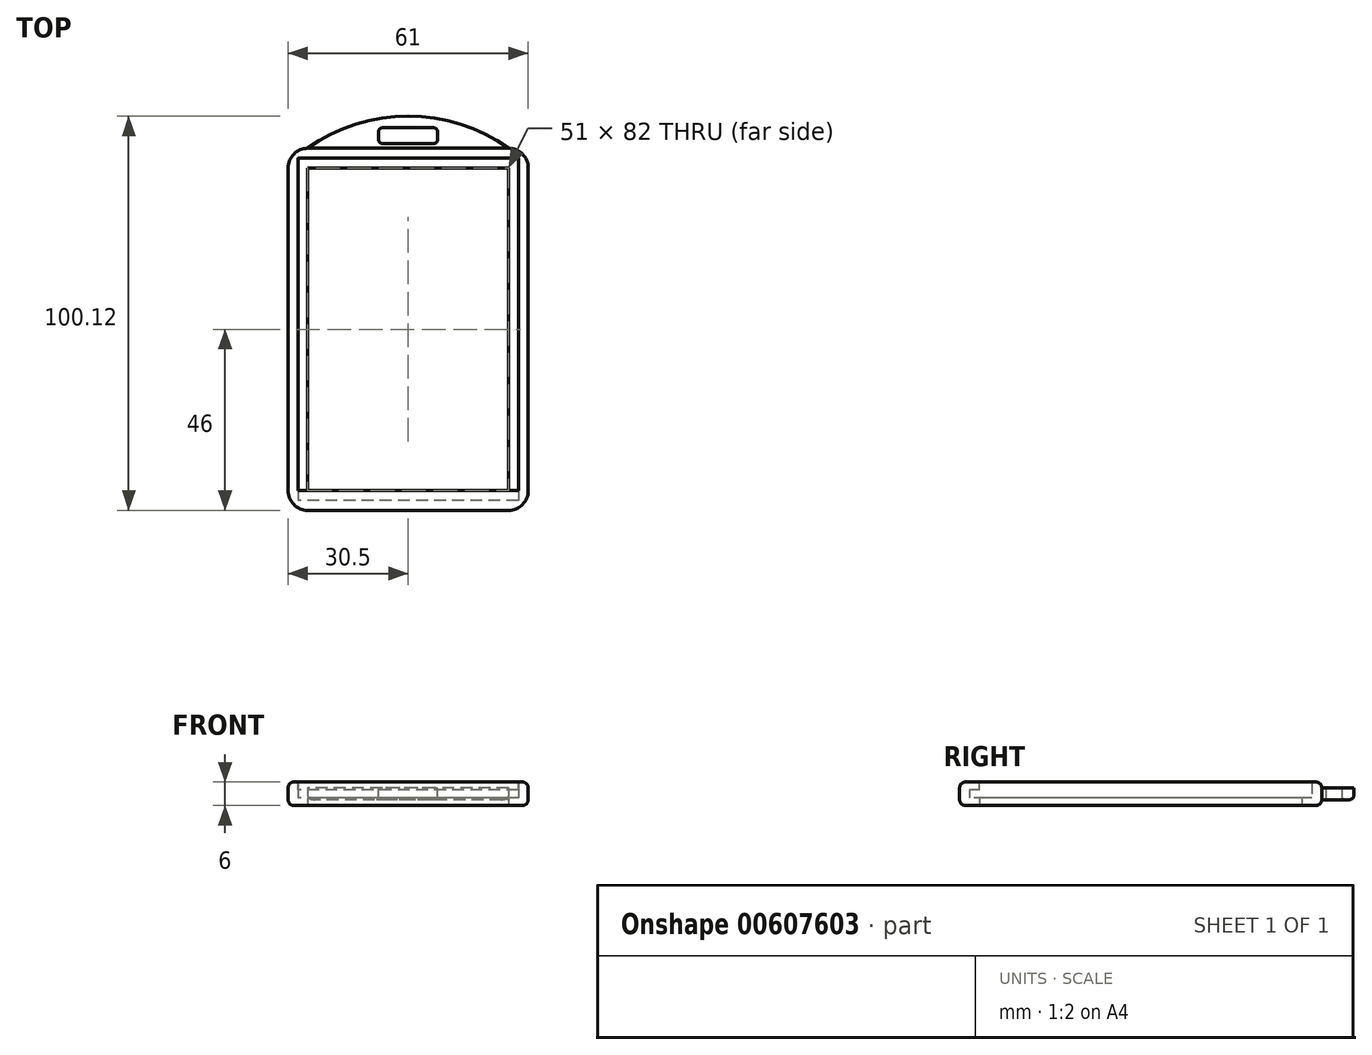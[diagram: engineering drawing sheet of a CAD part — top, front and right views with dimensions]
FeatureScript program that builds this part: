
annotation { "Feature Type Name" : "Feature", "Feature Type Description" : "" }
export const myFeature = defineFeature(function(context is Context, id is Id, definition is map)
    precondition{}
    {
        {
            assignVariable(context, id + "F0", {"name" : "CardThickness", "anyValue" : 2});
        }
        {
            assignVariable(context, id + "F1", {"name" : "LipThickness", "anyValue" : 2});
        }
        {
            var Q0;
            Q0=qCreatedBy(makeId("Top.planeOp"),FACE);
            var sketch = newSketch(context, id + "F2", { "sketchPlane" : qUnion([Q0])});
            skLineSegment(sketch, "E0.bottom", {"start": v(28, 43.5) * mm, "end": v(-28, 43.5) * mm});
            skLineSegment(sketch, "E0.top", {"start": v(28, -43.5) * mm, "end": v(-28, -43.5) * mm});
            skLineSegment(sketch, "E0.left", {"start": v(28, 43.5) * mm, "end": v(28, -43.5) * mm});
            skLineSegment(sketch, "E0.right", {"start": v(-28, 43.5) * mm, "end": v(-28, -43.5) * mm});
            skPoint(sketch, "E0.middle", {"position": v(0, 0) * mm});
            skLineSegment(sketch, "E1.0", {"start": v(25.5, 46) * mm, "end": v(-25.5, 46) * mm});
            skLineSegment(sketch, "E1.1", {"start": v(30.5, 41) * mm, "end": v(30.5, -41) * mm});
            skLineSegment(sketch, "E1.2", {"start": v(25.5, -46) * mm, "end": v(-25.5, -46) * mm});
            skLineSegment(sketch, "E1.3", {"start": v(-30.5, 41) * mm, "end": v(-30.5, -41) * mm});
            skPoint(sketch, "E2.visualSharp", {"position": v(-30.5, 46) * mm});
            skArc(sketch, "E2.filletArc", {"start": v(-25.5, 46) * mm, "mid": v(-29.04, 44.54) * mm, "end": v(-30.5, 41) * mm});
            skPoint(sketch, "E3.visualSharp", {"position": v(30.5, 46) * mm});
            skArc(sketch, "E3.filletArc", {"start": v(30.5, 41) * mm, "mid": v(29.04, 44.54) * mm, "end": v(25.5, 46) * mm});
            skPoint(sketch, "E4.visualSharp", {"position": v(30.5, -46) * mm});
            skArc(sketch, "E4.filletArc", {"start": v(25.5, -46) * mm, "mid": v(29.04, -44.54) * mm, "end": v(30.5, -41) * mm});
            skPoint(sketch, "E5.visualSharp", {"position": v(-30.5, -46) * mm});
            skArc(sketch, "E5.filletArc", {"start": v(-30.5, -41) * mm, "mid": v(-29.04, -44.54) * mm, "end": v(-25.5, -46) * mm});
            skLineSegment(sketch, "E6.0", {"start": v(25.5, -41) * mm, "end": v(-25.5, -41) * mm});
            skLineSegment(sketch, "E6.1", {"start": v(25.5, 41) * mm, "end": v(25.5, -41) * mm});
            skLineSegment(sketch, "E6.2", {"start": v(25.5, 41) * mm, "end": v(-25.5, 41) * mm});
            skLineSegment(sketch, "E6.3", {"start": v(-25.5, 41) * mm, "end": v(-25.5, -41) * mm});
            skSolve(sketch);
        }
        {
            var Q0;
            Q0=makeQuery(id+"F2.imprint","IMPRINT",FACE,{"disambiguationData":[TD([[makeQuery(id+"F2.imprint","IMPRINT",EDGE,{"derivedFrom":sQuery(id+"F2.wireOp",EDGE,"E0.bottom")}),-1.0]])]});
            extrude(context, id + "F3", {"entities" : qUnion([Q0]), "depth" : ((getVariable(context, 'CardThickness') + (2 * getVariable(context, 'LipThickness')))) * mm, "offsetDistance" : 25 * mm});
        }
        {
            var Q0;
            Q0=makeQuery(id+"F2.imprint","IMPRINT",FACE,{"disambiguationData":[TD([[makeQuery(id+"F2.imprint","IMPRINT",EDGE,{"derivedFrom":sQuery(id+"F2.wireOp",EDGE,"E0.bottom")}),1.0]])]});
            extrude(context, id + "F4", {"entities" : qUnion([Q0]), "operationType" : NewBodyOperationType.ADD, "depth" : (getVariable(context, 'LipThickness')) * mm, "offsetDistance" : 25 * mm});
        }
        {
            var Q0;
            Q0=makeQuery(id+"F3.opExtrude","CAP_FACE",FACE,{"disambiguationData":[OSD([sQuery(id+"F2.wireOp",EDGE,"E0.bottom"),sQuery(id+"F2.wireOp",EDGE,"E0.top"),sQuery(id+"F2.wireOp",EDGE,"E0.left"),sQuery(id+"F2.wireOp",EDGE,"E0.right"),sQuery(id+"F2.wireOp",EDGE,"E1.0"),sQuery(id+"F2.wireOp",EDGE,"E1.1"),sQuery(id+"F2.wireOp",EDGE,"E1.2"),sQuery(id+"F2.wireOp",EDGE,"E1.3"),sQuery(id+"F2.wireOp",EDGE,"E2.filletArc"),sQuery(id+"F2.wireOp",EDGE,"E3.filletArc"),sQuery(id+"F2.wireOp",EDGE,"E4.filletArc"),sQuery(id+"F2.wireOp",EDGE,"E5.filletArc")])],"isStart":false});
            var sketch = newSketch(context, id + "F5", { "sketchPlane" : qUnion([Q0])});
            skLineSegment(sketch, "E7.bottom", {"start": v(-28, -43.5) * mm, "end": v(28, -43.5) * mm});
            skLineSegment(sketch, "E7.top", {"start": v(-28, -41) * mm, "end": v(28, -41) * mm});
            skLineSegment(sketch, "E7.left", {"start": v(-28, -43.5) * mm, "end": v(-28, -41) * mm});
            skLineSegment(sketch, "E7.right", {"start": v(28, -43.5) * mm, "end": v(28, -41) * mm});
            skLineSegment(sketch, "E8.bottom", {"start": v(-28, -41) * mm, "end": v(-25.5, -41) * mm});
            skLineSegment(sketch, "E8.top", {"start": v(-28, 0) * mm, "end": v(-25.5, 0) * mm});
            skLineSegment(sketch, "E8.left", {"start": v(-28, -41) * mm, "end": v(-28, 0) * mm});
            skLineSegment(sketch, "E8.right", {"start": v(-25.5, -41) * mm, "end": v(-25.5, 0) * mm});
            skLineSegment(sketch, "E9.bottom", {"start": v(28, -41) * mm, "end": v(25.5, -41) * mm});
            skLineSegment(sketch, "E9.top", {"start": v(28, 0) * mm, "end": v(25.5, 0) * mm});
            skLineSegment(sketch, "E9.left", {"start": v(28, -41) * mm, "end": v(28, 0) * mm});
            skLineSegment(sketch, "E9.right", {"start": v(25.5, -41) * mm, "end": v(25.5, 0) * mm});
            skSolve(sketch);
        }
        {
            var Q0;
            Q0=makeQuery(id+"F5.imprint","IMPRINT",FACE,{"disambiguationData":[TD([[makeQuery(id+"F5.imprint","IMPRINT",EDGE,{"derivedFrom":sQuery(id+"F5.wireOp",EDGE,"E8.bottom")}),1.0]])]});
            var Q1;
            Q1=makeQuery(id+"F5.imprint","IMPRINT",FACE,{"disambiguationData":[TD([[makeQuery(id+"F5.imprint","IMPRINT",EDGE,{"derivedFrom":sQuery(id+"F5.wireOp",EDGE,"E7.bottom")}),-1.0]])]});
            var Q2;
            Q2=makeQuery(id+"F5.imprint","IMPRINT",FACE,{"disambiguationData":[TD([[makeQuery(id+"F5.imprint","IMPRINT",EDGE,{"derivedFrom":sQuery(id+"F5.wireOp",EDGE,"E9.bottom")}),-1.0]])]});
            extrude(context, id + "F6", {"entities" : qUnion([Q0, Q1, Q2]), "operationType" : NewBodyOperationType.ADD, "oppositeDirection" : true, "depth" : getVariable(context, 'LipThickness') * mm, "offsetDistance" : 25 * mm});
        }
        {
            var Q0;
            Q0=makeQuery(id+"F3.opExtrude","CAP_EDGE",EDGE,{"disambiguationData":[OSD([sQuery(id+"F2.wireOp",EDGE,"E1.3")])],"isStart":false});
            var Q1;
            Q1=makeQuery(id+"F3.opExtrude","CAP_EDGE",EDGE,{"disambiguationData":[OSD([sQuery(id+"F2.wireOp",EDGE,"E1.1")])],"isStart":true});
            fillet(context, id + "F7", {"entities" : qUnion([Q0, Q1]), "radius" : 1.5 * mm, "tangentPropagation" : true, "allowEdgeOverflow" : false});
        }
        {
            var Q0;
            Q0=makeQuery(id+"F3.opExtrude","SWEPT_FACE",FACE,{"disambiguationData":[OSD([sQuery(id+"F2.wireOp",EDGE,"E1.0")])]});
            extrude(context, id + "F8", {"entities" : qUnion([Q0]), "operationType" : NewBodyOperationType.ADD, "depth" : 10 * mm, "offsetDistance" : 25 * mm});
        }
        {
            var Q0;
            {var subQ0=sQuery(id+"F2.wireOp",EDGE,"E1.0");Q0=makeQuery(id+"F8.opExtrude","SWEPT_FACE",FACE,{"disambiguationData":[OSD([subQ0]),TDD([makeQuery(id+"F7.opFillet","BLEND_EDGE",EDGE,{"blendedFrom":[makeQuery(id+"F3.opExtrude","CAP_EDGE",EDGE,{"disambiguationData":[OSD([subQ0])],"isStart":false}),makeQuery(id+"F3.opExtrude","SWEPT_FACE",FACE,{"disambiguationData":[OSD([subQ0])]})],"blendedInto":[makeQuery(id+"F3.opExtrude","SWEPT_FACE",FACE,{"disambiguationData":[OSD([subQ0])]})]})])]});}
            var sketch = newSketch(context, id + "F9", { "sketchPlane" : qUnion([Q0])});
            skLineSegment(sketch, "E10.bottom", {"start": v(7.5, 51.2) * mm, "end": v(-7.5, 51.2) * mm});
            skLineSegment(sketch, "E10.top", {"start": v(7.5, 47.2) * mm, "end": v(-7.5, 47.2) * mm});
            skLineSegment(sketch, "E10.left", {"start": v(7.5, 51.2) * mm, "end": v(7.5, 47.2) * mm});
            skLineSegment(sketch, "E10.right", {"start": v(-7.5, 51.2) * mm, "end": v(-7.5, 47.2) * mm});
            skArc(sketch, "E11", {"start": v(25.5, 46) * mm, "mid": v(0, 54.12) * mm, "end": v(-25.5, 46) * mm});
            skSolve(sketch);
        }
        {
            var Q0;
            Q0=makeQuery(id+"F9.imprint","IMPRINT",FACE,{"disambiguationData":[TD([[makeQuery(id+"F9.imprint","IMPRINT",EDGE,{"derivedFrom":sQuery(id+"F9.wireOp",EDGE,"E11")}),-1.0]])]});
            extrude(context, id + "F10", {"entities" : qUnion([Q0]), "operationType" : NewBodyOperationType.REMOVE, "oppositeDirection" : true, "depth" : 25 * mm, "offsetDistance" : 25 * mm});
        }
        {
            var Q0;
            Q0 = qSketchRegion(id + "F9", true);
            extrude(context, id + "F11", {"entities" : qUnion([Q0]), "operationType" : NewBodyOperationType.REMOVE, "oppositeDirection" : true, "depth" : 25 * mm, "offsetDistance" : 25 * mm});
        }
        {
            var Q0;
            {var subQ0=sQuery(id+"F2.wireOp",EDGE,"E1.0");Q0=makeQuery(id+"F10.boolean.opBoolean","INTERSECT",EDGE,{"derivedFrom":[makeQuery(id+"F8.opExtrude","SWEPT_FACE",FACE,{"disambiguationData":[OSD([subQ0]),TDD([makeQuery(id+"F7.opFillet","BLEND_EDGE",EDGE,{"blendedFrom":[makeQuery(id+"F3.opExtrude","CAP_EDGE",EDGE,{"disambiguationData":[OSD([subQ0])],"isStart":true}),makeQuery(id+"F3.opExtrude","SWEPT_FACE",FACE,{"disambiguationData":[OSD([subQ0])]})],"blendedInto":[makeQuery(id+"F3.opExtrude","SWEPT_FACE",FACE,{"disambiguationData":[OSD([subQ0])]})]})])]}),makeQuery(id+"F10.opExtrude","SWEPT_FACE",FACE,{"disambiguationData":[OSD([sQuery(id+"F9.wireOp",EDGE,"E11")])]})]});}
            var Q1;
            Q1=makeQuery(id+"F10.boolean.opBoolean","COPY",EDGE,{"derivedFrom":makeQuery(id+"F10.opExtrude","CAP_EDGE",EDGE,{"disambiguationData":[OSD([sQuery(id+"F9.wireOp",EDGE,"E11")])],"isStart":true})});
            fillet(context, id + "F12", {"entities" : qUnion([Q0, Q1]), "radius" : 1 * mm, "tangentPropagation" : true, "allowEdgeOverflow" : false});
        }
        {
            var Q0;
            Q0=makeQuery(id+"F11.boolean.opBoolean","COPY",EDGE,{"derivedFrom":makeQuery(id+"F11.opExtrude","SWEPT_EDGE",EDGE,{"disambiguationData":[OSD([sQuery(id+"F9.wireOp",EDGE,"E10.bottom"),sQuery(id+"F9.wireOp",EDGE,"E10.right")])]})});
            var Q1;
            Q1=makeQuery(id+"F11.boolean.opBoolean","COPY",EDGE,{"derivedFrom":makeQuery(id+"F11.opExtrude","SWEPT_EDGE",EDGE,{"disambiguationData":[OSD([sQuery(id+"F9.wireOp",EDGE,"E10.bottom"),sQuery(id+"F9.wireOp",EDGE,"E10.left")])]})});
            var Q2;
            Q2=makeQuery(id+"F11.boolean.opBoolean","COPY",EDGE,{"derivedFrom":makeQuery(id+"F11.opExtrude","SWEPT_EDGE",EDGE,{"disambiguationData":[OSD([sQuery(id+"F9.wireOp",EDGE,"E10.top"),sQuery(id+"F9.wireOp",EDGE,"E10.left")])]})});
            var Q3;
            Q3=makeQuery(id+"F11.boolean.opBoolean","COPY",EDGE,{"derivedFrom":makeQuery(id+"F11.opExtrude","SWEPT_EDGE",EDGE,{"disambiguationData":[OSD([sQuery(id+"F9.wireOp",EDGE,"E10.top"),sQuery(id+"F9.wireOp",EDGE,"E10.right")])]})});
            fillet(context, id + "F13", {"entities" : qUnion([Q0, Q1, Q2, Q3]), "radius" : 1 * mm, "tangentPropagation" : true, "allowEdgeOverflow" : false});
        }
        {
            var Q0;
            Q0=makeQuery(id+"F11.boolean.opBoolean","COPY",EDGE,{"derivedFrom":makeQuery(id+"F11.opExtrude","CAP_EDGE",EDGE,{"disambiguationData":[OSD([sQuery(id+"F9.wireOp",EDGE,"E10.bottom")])],"isStart":true})});
            var Q1;
            {var subQ0=sQuery(id+"F2.wireOp",EDGE,"E1.0");Q1=makeQuery(id+"F11.boolean.opBoolean","INTERSECT",EDGE,{"derivedFrom":[makeQuery(id+"F8.opExtrude","SWEPT_FACE",FACE,{"disambiguationData":[OSD([subQ0]),TDD([makeQuery(id+"F7.opFillet","BLEND_EDGE",EDGE,{"blendedFrom":[makeQuery(id+"F3.opExtrude","CAP_EDGE",EDGE,{"disambiguationData":[OSD([subQ0])],"isStart":true}),makeQuery(id+"F3.opExtrude","SWEPT_FACE",FACE,{"disambiguationData":[OSD([subQ0])]})],"blendedInto":[makeQuery(id+"F3.opExtrude","SWEPT_FACE",FACE,{"disambiguationData":[OSD([subQ0])]})]})])]}),makeQuery(id+"F11.opExtrude","SWEPT_FACE",FACE,{"disambiguationData":[OSD([sQuery(id+"F9.wireOp",EDGE,"E10.bottom")])]})]});}
            fillet(context, id + "F14", {"entities" : qUnion([Q0, Q1]), "radius" : .5 * mm, "tangentPropagation" : true, "allowEdgeOverflow" : false});
        }
    });
